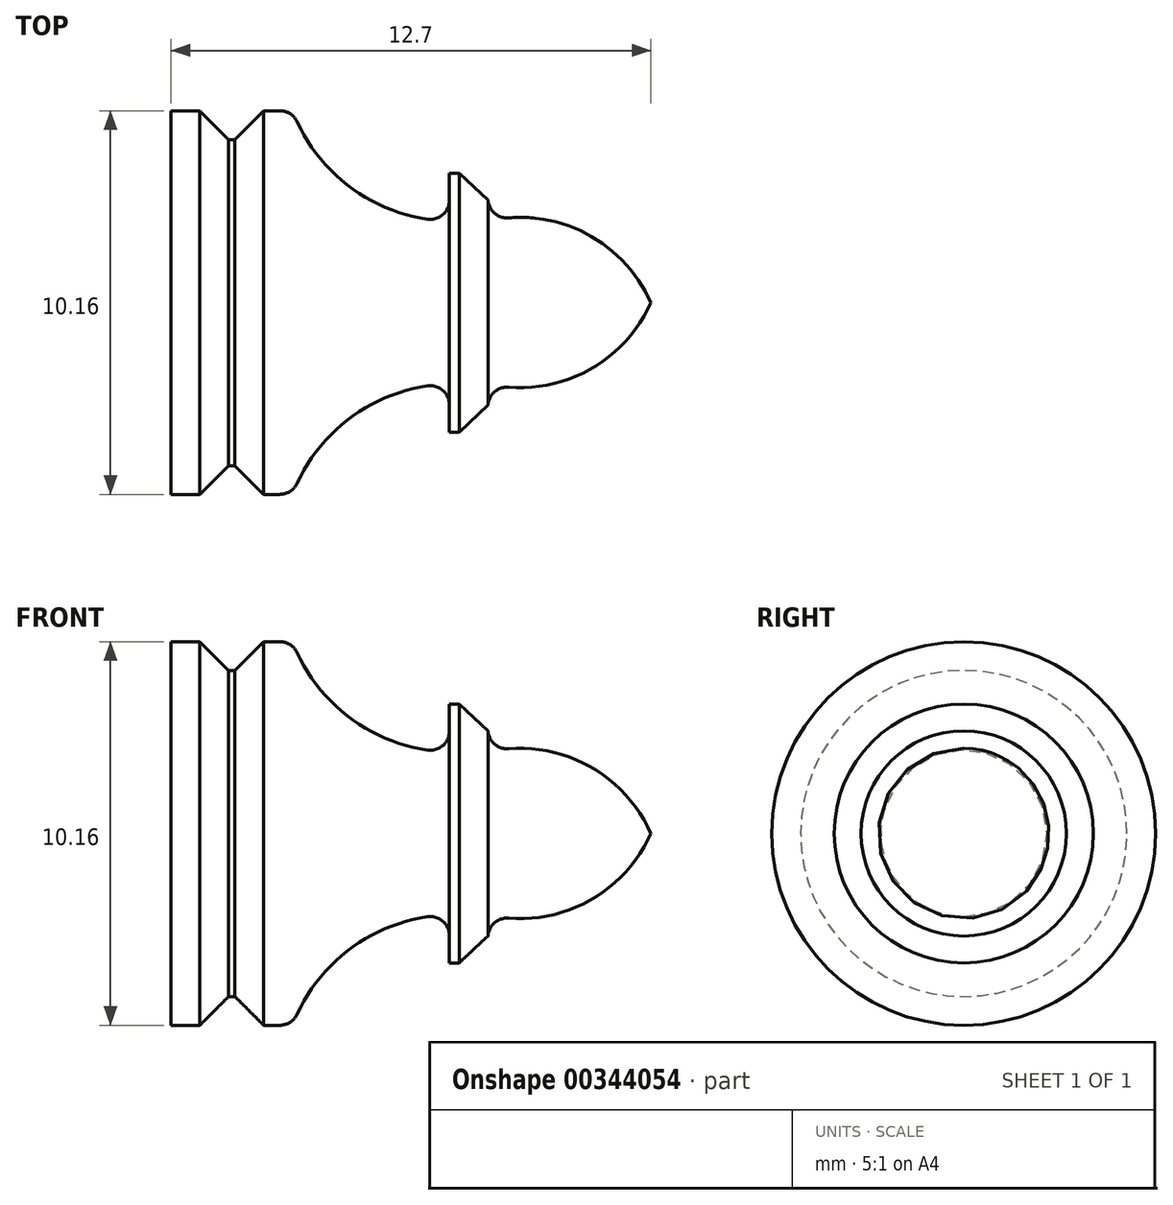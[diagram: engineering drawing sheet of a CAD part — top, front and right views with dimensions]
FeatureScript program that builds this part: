
annotation { "Feature Type Name" : "Feature", "Feature Type Description" : "" }
export const myFeature = defineFeature(function(context is Context, id is Id, definition is map)
    precondition{}
    {
        {
            var Q0;
            Q0=qCreatedBy(makeId("Front.planeOp"),FACE);
            var sketch = newSketch(context, id + "F0", { "sketchPlane" : qUnion([Q0])});
            skLineSegment(sketch, "E0", {"start": v(0, 0) * mm, "end": v(-12.7, 0) * mm});
            skLineSegment(sketch, "E1", {"start": v(-12.7, 0) * mm, "end": v(-12.7, 5.08) * mm});
            skLineSegment(sketch, "E2", {"start": v(-12.7, 5.08) * mm, "end": v(-11.18, 5.08) * mm});
            skLineSegment(sketch, "E3", {"start": v(-11.18, 5.08) * mm, "end": v(-11.18, 4.32) * mm});
            skLineSegment(sketch, "E4", {"start": v(-11.18, 4.32) * mm, "end": v(-11.01, 4.32) * mm});
            skLineSegment(sketch, "E5", {"start": v(-11.01, 4.32) * mm, "end": v(-11.01, 5.08) * mm});
            skLineSegment(sketch, "E6", {"start": v(-11.01, 5.08) * mm, "end": v(-9.49, 5.08) * mm});
            skArc(sketch, "E7", {"start": v(-9.49, 5.08) * mm, "mid": v(-7.86, 2.98) * mm, "end": v(-5.33, 2.16) * mm});
            skLineSegment(sketch, "E8", {"start": v(-5.33, 2.16) * mm, "end": v(-5.33, 3.43) * mm});
            skLineSegment(sketch, "E9", {"start": v(-5.33, 3.43) * mm, "end": v(-4.32, 3.43) * mm});
            skLineSegment(sketch, "E10", {"start": v(-4.32, 3.43) * mm, "end": v(-4.32, 2.16) * mm});
            skArc(sketch, "E11", {"start": v(0, 0) * mm, "mid": v(-1.77, 1.86) * mm, "end": v(-4.32, 2.16) * mm});
            skSolve(sketch);
        }
        {
            var Q0;
            Q0=makeQuery(id+"F0.imprint","IMPRINT",FACE,{"disambiguationData":[TD([[makeQuery(id+"F0.imprint","IMPRINT",EDGE,{"derivedFrom":sQuery(id+"F0.wireOp",EDGE,"E0")}),-1.0]])]});
            var Q1;
            Q1=sQuery(id+"F0.wireOp",EDGE,"E0");
            revolve(context, id + "F1", {"entities" : qUnion([Q0]), "axis" : qUnion([Q1]), "revolveType" : RevolveType.FULL});
        }
        {
            var Q0;
            Q0=makeQuery(id+"F1.opRevolve","SWEPT_FACE",FACE,{"disambiguationData":[OSD([sQuery(id+"F0.wireOp",EDGE,"E11")])]});
            var Q1;
            Q1=makeQuery(id+"F1.opRevolve","SWEPT_FACE",FACE,{"disambiguationData":[OSD([sQuery(id+"F0.wireOp",EDGE,"E7")])]});
            fillet(context, id + "F2", {"entities" : qUnion([Q0, Q1]), "radius" : 0.5 * mm, "tangentPropagation" : true, "allowEdgeOverflow" : false});
        }
        {
            var Q0;
            Q0=makeQuery(id+"F1.opRevolve","SWEPT_EDGE",EDGE,{"disambiguationData":[OSD([sQuery(id+"F0.wireOp",EDGE,"E9"),sQuery(id+"F0.wireOp",EDGE,"E10")])]});
            var Q1;
            Q1=makeQuery(id+"F1.opRevolve","SWEPT_EDGE",EDGE,{"disambiguationData":[OSD([sQuery(id+"F0.wireOp",EDGE,"E2"),sQuery(id+"F0.wireOp",EDGE,"E3")])]});
            var Q2;
            Q2=makeQuery(id+"F1.opRevolve","SWEPT_EDGE",EDGE,{"disambiguationData":[OSD([sQuery(id+"F0.wireOp",EDGE,"E5"),sQuery(id+"F0.wireOp",EDGE,"E6")])]});
            chamfer(context, id + "F3", {"entities" : qUnion([Q0, Q1, Q2]), "width" : 0.76 * mm, "tangentPropagation" : true});
        }
    });
